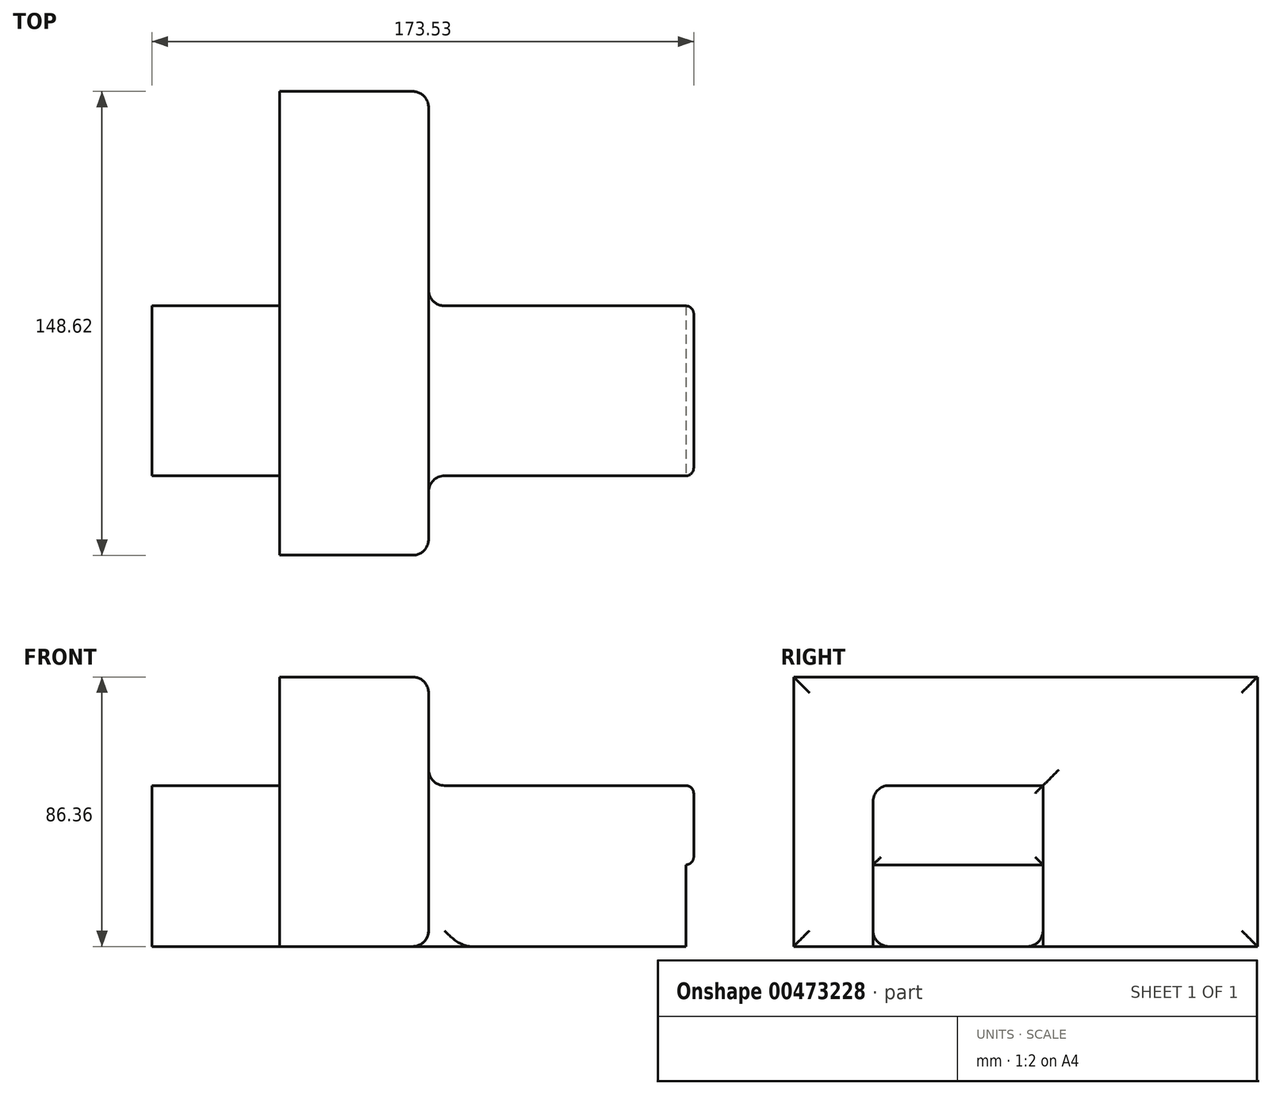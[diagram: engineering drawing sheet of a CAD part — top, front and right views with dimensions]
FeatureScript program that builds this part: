
annotation { "Feature Type Name" : "Feature", "Feature Type Description" : "" }
export const myFeature = defineFeature(function(context is Context, id is Id, definition is map)
    precondition{}
    {
        {
            var Q0;
            Q0=qCreatedBy(makeId("Top.planeOp"),FACE);
            var sketch = newSketch(context, id + "F0", { "sketchPlane" : qUnion([Q0])});
            skLineSegment(sketch, "E0.bottom", {"start": v(-40.87, 32.02) * mm, "end": v(132.66, 32.02) * mm});
            skLineSegment(sketch, "E0.top", {"start": v(-40.87, -22.43) * mm, "end": v(132.66, -22.43) * mm});
            skLineSegment(sketch, "E0.left", {"start": v(-40.87, 32.02) * mm, "end": v(-40.87, -22.43) * mm});
            skLineSegment(sketch, "E0.right", {"start": v(132.66, 32.02) * mm, "end": v(132.66, -22.43) * mm});
            skSolve(sketch);
        }
        {
            var Q0;
            Q0=makeQuery(id+"F0.imprint","IMPRINT",FACE,{"disambiguationData":[TD([[makeQuery(id+"F0.imprint","IMPRINT",EDGE,{"derivedFrom":sQuery(id+"F0.wireOp",EDGE,"E0.bottom")}),-1.0]])]});
            extrude(context, id + "F1", {"entities" : qUnion([Q0]), "depth" : 25.4 * mm});
        }
        {
            var Q0;
            Q0=makeQuery(id+"F1.opExtrude","CAP_EDGE",EDGE,{"disambiguationData":[OSD([sQuery(id+"F0.wireOp",EDGE,"E0.top")])],"isStart":false});
            fillet(context, id + "F2", {"entities" : qUnion([Q0]), "radius" : 5.08 * mm, "tangentPropagation" : true, "allowEdgeOverflow" : false});
        }
        {
            var Q0;
            Q0=makeQuery(id+"F1.opExtrude","SWEPT_FACE",FACE,{"disambiguationData":[OSD([sQuery(id+"F0.wireOp",EDGE,"E0.right")])]});
            fillet(context, id + "F3", {"entities" : qUnion([Q0]), "radius" : 2.54 * mm, "tangentPropagation" : true, "allowEdgeOverflow" : false});
        }
        {
            var Q0;
            Q0=qCreatedBy(makeId("Top.planeOp"),FACE);
            var sketch = newSketch(context, id + "F4", { "sketchPlane" : qUnion([Q0])});
            skLineSegment(sketch, "E1.bottom", {"start": v(47.73, -47.89) * mm, "end": v(0, -47.89) * mm});
            skLineSegment(sketch, "E1.top", {"start": v(47.73, 100.73) * mm, "end": v(0, 100.73) * mm});
            skLineSegment(sketch, "E1.left", {"start": v(47.73, -47.89) * mm, "end": v(47.73, 100.73) * mm});
            skLineSegment(sketch, "E1.right", {"start": v(0, -47.89) * mm, "end": v(0, 100.73) * mm});
            skSolve(sketch);
        }
        {
            var Q0;
            Q0=makeQuery(id+"F4.imprint","IMPRINT",FACE,{"disambiguationData":[TD([[makeQuery(id+"F4.imprint","IMPRINT",EDGE,{"derivedFrom":sQuery(id+"F4.wireOp",EDGE,"E1.bottom")}),-1.0]])]});
            extrude(context, id + "F5", {"entities" : qUnion([Q0]), "operationType" : NewBodyOperationType.ADD, "depth" : 60.2 * mm});
        }
        {
            var Q0;
            Q0=makeQuery(id+"F5.boolean.opBoolean","MERGE",FACE,{"derivedFrom":[makeQuery(id+"F1.opExtrude","CAP_FACE",FACE,{"disambiguationData":[OSD([sQuery(id+"F0.wireOp",EDGE,"E0.bottom"),sQuery(id+"F0.wireOp",EDGE,"E0.top"),sQuery(id+"F0.wireOp",EDGE,"E0.left"),sQuery(id+"F0.wireOp",EDGE,"E0.right")])],"isStart":true}),makeQuery(id+"F5.opExtrude","CAP_FACE",FACE,{"disambiguationData":[OSD([sQuery(id+"F4.wireOp",EDGE,"E1.bottom"),sQuery(id+"F4.wireOp",EDGE,"E1.top"),sQuery(id+"F4.wireOp",EDGE,"E1.left"),sQuery(id+"F4.wireOp",EDGE,"E1.right")])],"isStart":true})]});
            extrude(context, id + "F6", {"entities" : qUnion([Q0]), "operationType" : NewBodyOperationType.ADD, "depth" : 26.16 * mm});
        }
        {
            var Q0;
            {var subQ1=sQuery(id+"F0.wireOp",EDGE,"E0.top");var subQ2=sQuery(id+"F0.wireOp",EDGE,"E0.bottom");var subQ4=sQuery(id+"F4.wireOp",EDGE,"E1.left");var subQ7=makeQuery(id+"F5.opExtrude","SWEPT_FACE",FACE,{"disambiguationData":[OSD([subQ4])]});var subQ8=makeQuery(id+"F5.opExtrude","CAP_EDGE",EDGE,{"disambiguationData":[OSD([subQ4])],"isStart":true});Q0=makeQuery(id+"F6.boolean.opBoolean","MERGE",FACE,{"derivedFrom":[subQ7,makeQuery(id+"F6.opExtrude","SWEPT_FACE",FACE,{"disambiguationData":[OSD([subQ4]),TDD([makeQuery(id+"F5.boolean.opBoolean","SPLIT",EDGE,{"disambiguationData":[TD([makeQuery(id+"F1.opExtrude","SWEPT_FACE",FACE,{"disambiguationData":[OSD([subQ1])]})])],"derivedFrom":subQ8})])]}),makeQuery(id+"F6.opExtrude","SWEPT_FACE",FACE,{"disambiguationData":[OSD([subQ4]),TDD([makeQuery(id+"F5.boolean.opBoolean","SPLIT",EDGE,{"disambiguationData":[TD([makeQuery(id+"F1.opExtrude","SWEPT_FACE",FACE,{"disambiguationData":[OSD([subQ2])]})])],"derivedFrom":subQ8})])]})]});}
            fillet(context, id + "F7", {"entities" : qUnion([Q0]), "radius" : 5.08 * mm, "tangentPropagation" : true, "allowEdgeOverflow" : false});
        }
    });
